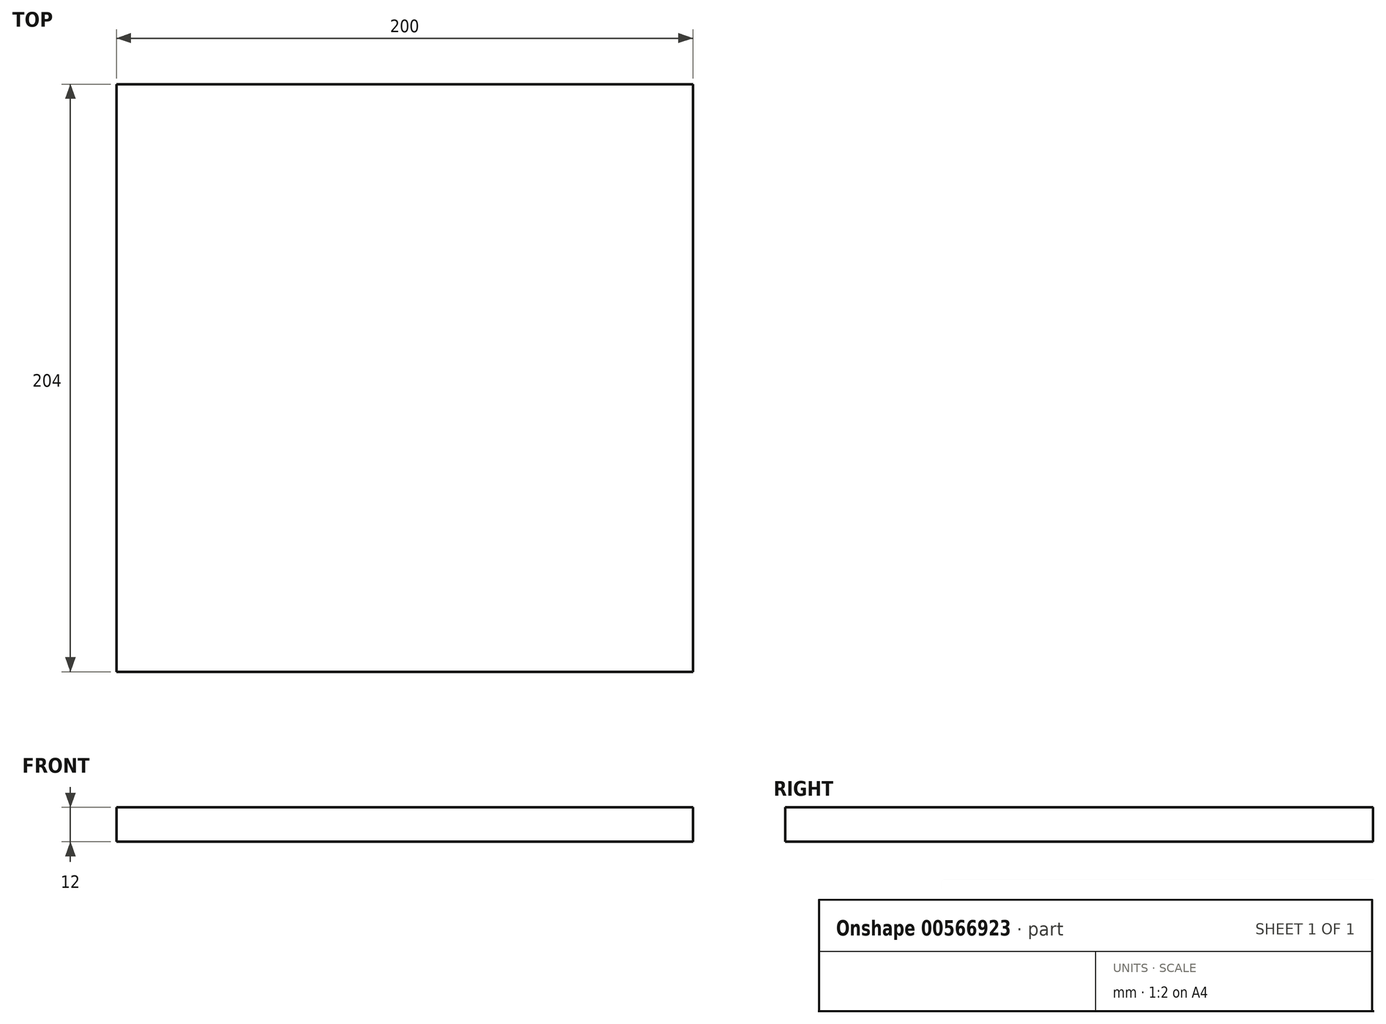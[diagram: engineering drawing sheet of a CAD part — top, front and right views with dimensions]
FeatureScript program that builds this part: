
annotation { "Feature Type Name" : "Feature", "Feature Type Description" : "" }
export const myFeature = defineFeature(function(context is Context, id is Id, definition is map)
    precondition{}
    {
        {
            var Q0;
            Q0=qCreatedBy(makeId("Top.planeOp"),FACE);
            var sketch = newSketch(context, id + "F0", { "sketchPlane" : qUnion([Q0])});
            skLineSegment(sketch, "E0", {"start": v(0, 0) * mm, "end": v(200, 0) * mm});
            skLineSegment(sketch, "E1", {"start": v(200, 0) * mm, "end": v(200, -204) * mm});
            skLineSegment(sketch, "E2", {"start": v(200, -204) * mm, "end": v(0, -204) * mm});
            skLineSegment(sketch, "E3", {"start": v(0, -204) * mm, "end": v(0, 0) * mm});
            skSolve(sketch);
        }
        {
            var Q0;
            Q0 = qSketchRegion(id + "F0", true);
            extrude(context, id + "F1", {"entities" : qUnion([Q0]), "depth" : 12 * mm, "offsetDistance" : 25 * mm});
        }
    });
